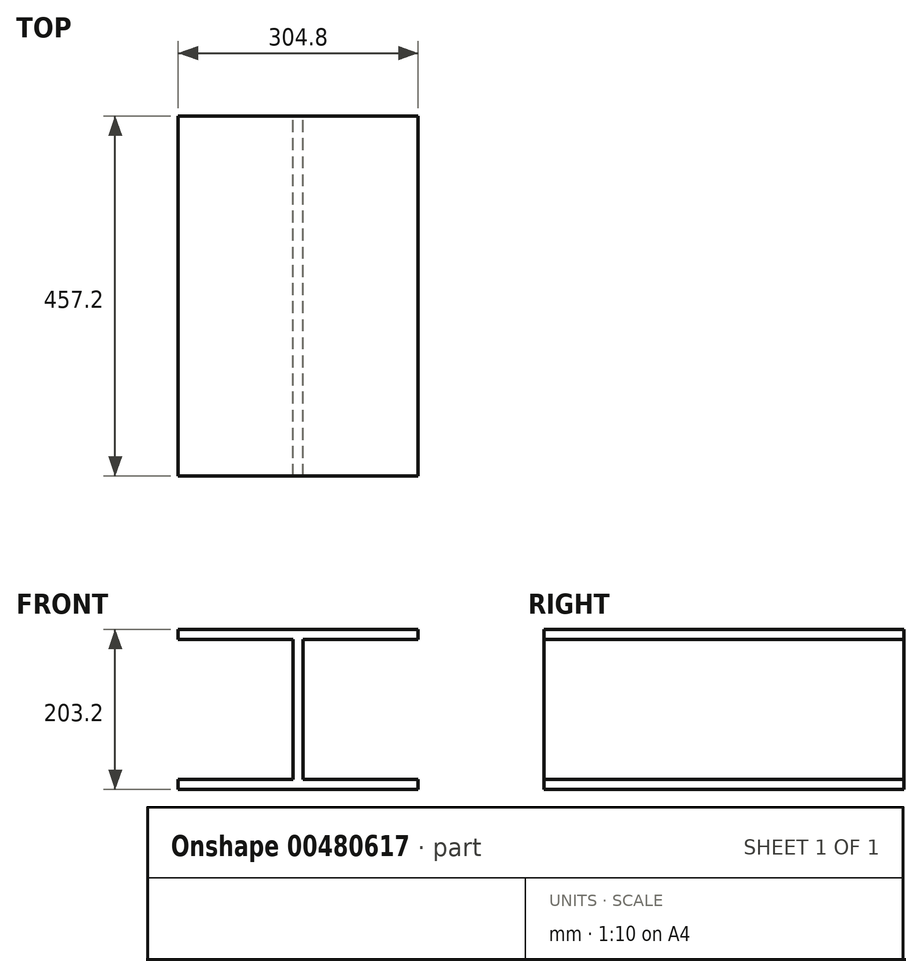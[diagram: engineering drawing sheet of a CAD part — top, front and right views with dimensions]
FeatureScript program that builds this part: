
annotation { "Feature Type Name" : "Feature", "Feature Type Description" : "" }
export const myFeature = defineFeature(function(context is Context, id is Id, definition is map)
    precondition{}
    {
        {
            var Q0;
            Q0=qCreatedBy(makeId("Front.planeOp"),FACE);
            var sketch = newSketch(context, id + "F0", { "sketchPlane" : qUnion([Q0])});
            skLineSegment(sketch, "E0.bottom", {"start": v(152.4, 101.6) * mm, "end": v(-152.4, 101.6) * mm});
            skLineSegment(sketch, "E0.top", {"start": v(152.4, -101.6) * mm, "end": v(-152.4, -101.6) * mm});
            skLineSegment(sketch, "E0.left", {"start": v(152.4, 101.6) * mm, "end": v(152.4, 88.9) * mm});
            skLineSegment(sketch, "E0.right", {"start": v(-152.4, 101.6) * mm, "end": v(-152.4, 88.9) * mm});
            skPoint(sketch, "E0.middle", {"position": v(0, 0) * mm});
            skLineSegment(sketch, "E1.0", {"start": v(152.4, 88.9) * mm, "end": v(6.35, 88.9) * mm});
            skLineSegment(sketch, "E1.2", {"start": v(152.4, -88.9) * mm, "end": v(6.35, -88.9) * mm});
            skLineSegment(sketch, "E2.0", {"start": v(6.35, 88.9) * mm, "end": v(6.35, -88.9) * mm});
            skLineSegment(sketch, "E3.0", {"start": v(-6.35, 88.9) * mm, "end": v(-6.35, -88.9) * mm});
            skLineSegment(sketch, "E4.trimOffspring", {"start": v(152.4, -88.9) * mm, "end": v(152.4, -101.6) * mm});
            skLineSegment(sketch, "E5.trimOffspring", {"start": v(-152.4, -88.9) * mm, "end": v(-152.4, -101.6) * mm});
            skPoint(sketch, "E6.orphan", {"position": v(0, -101.6) * mm});
            skLineSegment(sketch, "E7.trimOffspring", {"start": v(-6.35, -88.9) * mm, "end": v(-152.4, -88.9) * mm});
            skLineSegment(sketch, "E8.trimOffspring", {"start": v(-6.35, 88.9) * mm, "end": v(-152.4, 88.9) * mm});
            skSolve(sketch);
        }
        {
            var Q0;
            Q0 = qSketchRegion(id + "F0", true);
            extrude(context, id + "F1", {"entities" : qUnion([Q0]), "depth" : 457.2 * mm});
        }
    });
